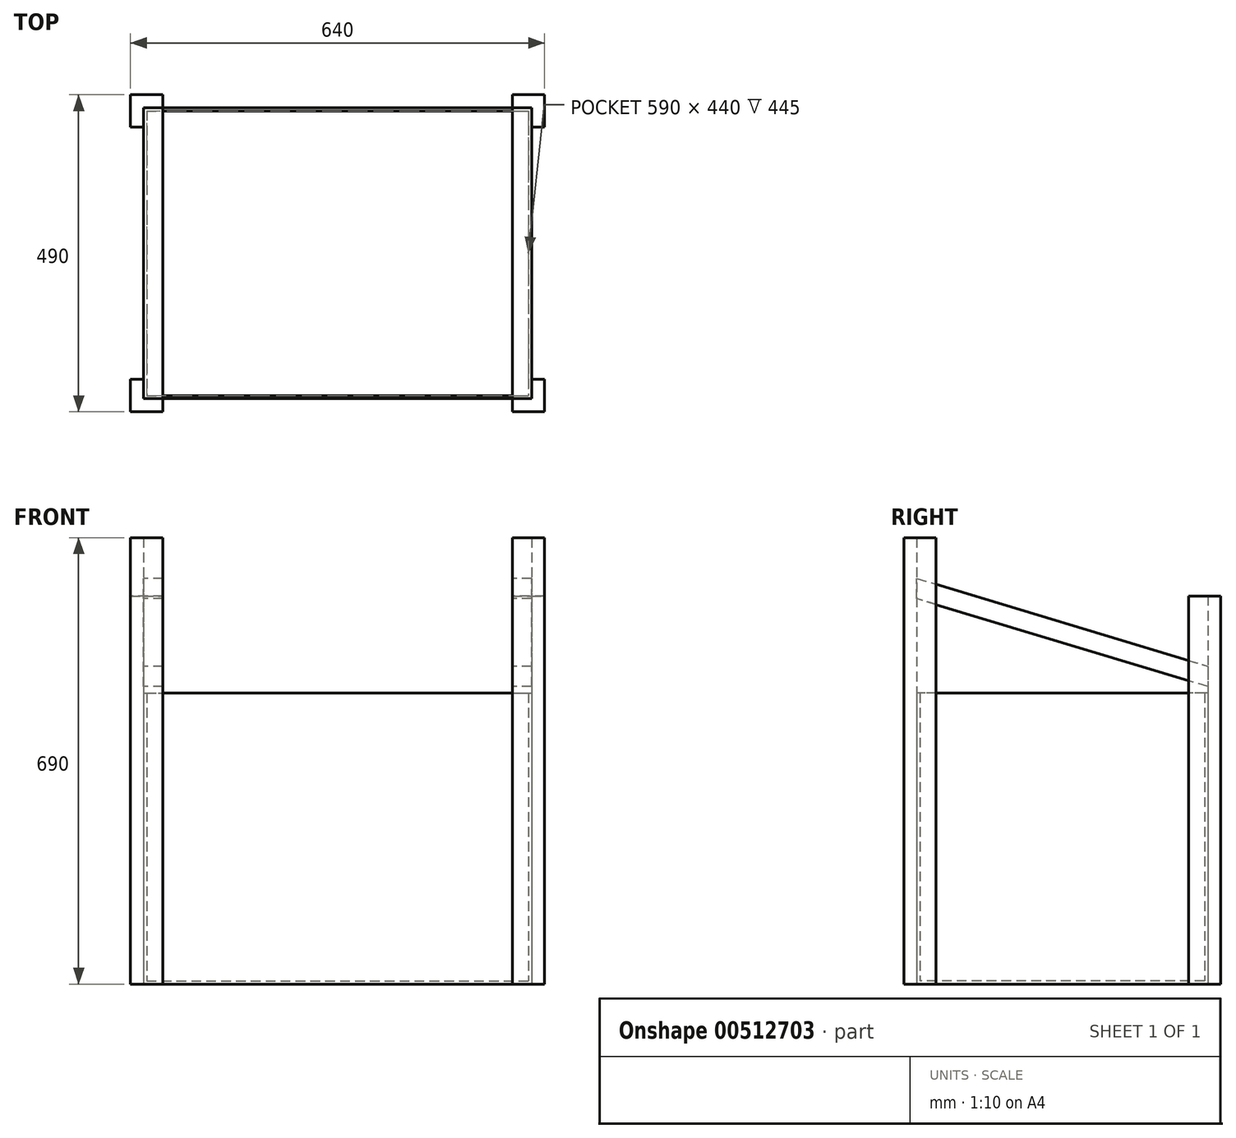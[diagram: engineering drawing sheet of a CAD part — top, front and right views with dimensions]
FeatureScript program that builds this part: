
annotation { "Feature Type Name" : "Feature", "Feature Type Description" : "" }
export const myFeature = defineFeature(function(context is Context, id is Id, definition is map)
    precondition{}
    {
        {
            var Q0;
            Q0=qCreatedBy(makeId("Top.planeOp"),FACE);
            var sketch = newSketch(context, id + "F0", { "sketchPlane" : qUnion([Q0])});
            skLineSegment(sketch, "E0.bottom", {"start": v(-300, 225) * mm, "end": v(300, 225) * mm});
            skLineSegment(sketch, "E0.top", {"start": v(-300, -225) * mm, "end": v(300, -225) * mm});
            skLineSegment(sketch, "E0.left", {"start": v(-300, 225) * mm, "end": v(-300, -225) * mm});
            skLineSegment(sketch, "E0.right", {"start": v(300, 225) * mm, "end": v(300, -225) * mm});
            skPoint(sketch, "E0.middle", {"position": v(0, 0) * mm});
            skSolve(sketch);
        }
        {
            var Q0;
            Q0 = qSketchRegion(id + "F0", true);
            extrude(context, id + "F1", {"entities" : qUnion([Q0]), "depth" : 450 * mm});
        }
        {
            var Q0;
            Q0=makeQuery(id+"F1.opExtrude","CAP_FACE",FACE,{"disambiguationData":[OSD([sQuery(id+"F0.wireOp",EDGE,"E0.bottom"),sQuery(id+"F0.wireOp",EDGE,"E0.top"),sQuery(id+"F0.wireOp",EDGE,"E0.left"),sQuery(id+"F0.wireOp",EDGE,"E0.right")])],"isStart":false});
            shell(context, id + "F2", {"entities" : qUnion([Q0]), "thickness" : 5 * mm});
        }
        {
            var Q0;
            Q0=makeQuery(id+"F1.opExtrude","CAP_FACE",FACE,{"disambiguationData":[OSD([sQuery(id+"F0.wireOp",EDGE,"E0.bottom"),sQuery(id+"F0.wireOp",EDGE,"E0.top"),sQuery(id+"F0.wireOp",EDGE,"E0.left"),sQuery(id+"F0.wireOp",EDGE,"E0.right")])],"isStart":true});
            var sketch = newSketch(context, id + "F3", { "sketchPlane" : qUnion([Q0])});
            skLineSegment(sketch, "E1", {"start": v(-300, 195) * mm, "end": v(-320, 195) * mm});
            skLineSegment(sketch, "E2", {"start": v(-320, 195) * mm, "end": v(-320, 245) * mm});
            skLineSegment(sketch, "E3", {"start": v(-320, 245) * mm, "end": v(-270, 245) * mm});
            skLineSegment(sketch, "E4", {"start": v(-270, 245) * mm, "end": v(-270, 225) * mm});
            skLineSegment(sketch, "E5", {"start": v(-270, 225) * mm, "end": v(-300, 225) * mm});
            skLineSegment(sketch, "E6", {"start": v(-300, 225) * mm, "end": v(-300, 195) * mm});
            skSolve(sketch);
        }
        {
            var Q0;
            Q0 = qSketchRegion(id + "F3", true);
            extrude(context, id + "F4", {"entities" : qUnion([Q0]), "oppositeDirection" : true, "depth" : 690 * mm});
        }
        {
            var Q0;
            Q0=makeQuery(id+"F4.opExtrude","SWEPT_BODY",BODY,{"disambiguationData":[OSD([sQuery(id+"F3.wireOp",EDGE,"E1"),sQuery(id+"F3.wireOp",EDGE,"E2"),sQuery(id+"F3.wireOp",EDGE,"E3"),sQuery(id+"F3.wireOp",EDGE,"E4"),sQuery(id+"F3.wireOp",EDGE,"E5"),sQuery(id+"F3.wireOp",EDGE,"E6")])]});
            transform(context, id + "F5", {"entities" : qUnion([Q0]), "transformType" : TransformType.TRANSLATION_3D, "dx" : 600 * mm, "dy" : 0 * mm, "dz" : 0 * mm, "makeCopy" : true});
        }
        {
            var Q0;
            Q0=makeQuery(id+"F5.opPattern","COPY",BODY,{"derivedFrom":makeQuery(id+"F4.opExtrude","SWEPT_BODY",BODY,{"disambiguationData":[OSD([sQuery(id+"F3.wireOp",EDGE,"E1"),sQuery(id+"F3.wireOp",EDGE,"E2"),sQuery(id+"F3.wireOp",EDGE,"E3"),sQuery(id+"F3.wireOp",EDGE,"E4"),sQuery(id+"F3.wireOp",EDGE,"E5"),sQuery(id+"F3.wireOp",EDGE,"E6")])]}),"instanceName":"1"});
            var Q1;
            Q1=makeQuery(id+"F1.opExtrude","SWEPT_EDGE",EDGE,{"disambiguationData":[OSD([sQuery(id+"F0.wireOp",EDGE,"E0.top"),sQuery(id+"F0.wireOp",EDGE,"E0.right")])]});
            transform(context, id + "F6", {"entities" : qUnion([Q0]), "transformType" : TransformType.ROTATION, "transformAxis" : qUnion([Q1]), "angle" : 90 * degree, "oppositeDirection" : true, "makeCopy" : false});
        }
        {
            var Q0;
            Q0=makeQuery(id+"F1.opExtrude","CAP_FACE",FACE,{"disambiguationData":[OSD([sQuery(id+"F0.wireOp",EDGE,"E0.bottom"),sQuery(id+"F0.wireOp",EDGE,"E0.top"),sQuery(id+"F0.wireOp",EDGE,"E0.left"),sQuery(id+"F0.wireOp",EDGE,"E0.right")])],"isStart":true});
            var sketch = newSketch(context, id + "F7", { "sketchPlane" : qUnion([Q0])});
            skLineSegment(sketch, "E7", {"start": v(300, -195) * mm, "end": v(320, -195) * mm});
            skLineSegment(sketch, "E8", {"start": v(320, -195) * mm, "end": v(320, -245) * mm});
            skLineSegment(sketch, "E9", {"start": v(320, -245) * mm, "end": v(270, -245) * mm});
            skLineSegment(sketch, "E10", {"start": v(270, -245) * mm, "end": v(270, -225) * mm});
            skLineSegment(sketch, "E11", {"start": v(270, -225) * mm, "end": v(300, -225) * mm});
            skLineSegment(sketch, "E12", {"start": v(300, -225) * mm, "end": v(300, -195) * mm});
            skSolve(sketch);
        }
        {
            var Q0;
            Q0 = qSketchRegion(id + "F7", true);
            extrude(context, id + "F8", {"entities" : qUnion([Q0]), "oppositeDirection" : true, "depth" : 600 * mm});
        }
        {
            var Q0;
            Q0=makeQuery(id+"F8.opExtrude","SWEPT_BODY",BODY,{"disambiguationData":[OSD([sQuery(id+"F7.wireOp",EDGE,"E7"),sQuery(id+"F7.wireOp",EDGE,"E8"),sQuery(id+"F7.wireOp",EDGE,"E9"),sQuery(id+"F7.wireOp",EDGE,"E10"),sQuery(id+"F7.wireOp",EDGE,"E11"),sQuery(id+"F7.wireOp",EDGE,"E12")])]});
            transform(context, id + "F9", {"entities" : qUnion([Q0]), "transformType" : TransformType.TRANSLATION_3D, "dx" : -600 * mm, "dy" : 0 * mm, "dz" : 0 * mm, "makeCopy" : true});
        }
        {
            var Q0;
            Q0=makeQuery(id+"F9.opPattern","COPY",BODY,{"derivedFrom":makeQuery(id+"F8.opExtrude","SWEPT_BODY",BODY,{"disambiguationData":[OSD([sQuery(id+"F7.wireOp",EDGE,"E7"),sQuery(id+"F7.wireOp",EDGE,"E8"),sQuery(id+"F7.wireOp",EDGE,"E9"),sQuery(id+"F7.wireOp",EDGE,"E10"),sQuery(id+"F7.wireOp",EDGE,"E11"),sQuery(id+"F7.wireOp",EDGE,"E12")])]}),"instanceName":"1"});
            var Q1;
            Q1=makeQuery(id+"F1.opExtrude","SWEPT_EDGE",EDGE,{"disambiguationData":[OSD([sQuery(id+"F0.wireOp",EDGE,"E0.bottom"),sQuery(id+"F0.wireOp",EDGE,"E0.left")])]});
            transform(context, id + "F10", {"entities" : qUnion([Q0]), "transformType" : TransformType.ROTATION, "transformAxis" : qUnion([Q1]), "angle" : 90 * degree, "oppositeDirection" : true, "makeCopy" : false});
        }
        {
            var Q0;
            Q0=makeQuery(id+"F1.opExtrude","SWEPT_FACE",FACE,{"disambiguationData":[OSD([sQuery(id+"F0.wireOp",EDGE,"E0.left")])]});
            var sketch = newSketch(context, id + "F11", { "sketchPlane" : qUnion([Q0])});
            skLineSegment(sketch, "E13", {"start": v(-225, 460) * mm, "end": v(225, 595.86) * mm});
            skLineSegment(sketch, "E14", {"start": v(225, 595.86) * mm, "end": v(225, 627.2) * mm});
            skLineSegment(sketch, "E15", {"start": v(225, 627.2) * mm, "end": v(-225, 491.34) * mm});
            skLineSegment(sketch, "E16", {"start": v(-225, 491.34) * mm, "end": v(-225, 460) * mm});
            skSolve(sketch);
        }
        {
            var Q0;
            Q0 = qSketchRegion(id + "F11", true);
            extrude(context, id + "F12", {"entities" : qUnion([Q0]), "oppositeDirection" : true, "depth" : 30 * mm});
        }
        {
            var Q0;
            Q0=makeQuery(id+"F12.opExtrude","SWEPT_BODY",BODY,{"disambiguationData":[OSD([sQuery(id+"F11.wireOp",EDGE,"E13"),sQuery(id+"F11.wireOp",EDGE,"E14"),sQuery(id+"F11.wireOp",EDGE,"E15"),sQuery(id+"F11.wireOp",EDGE,"E16")])]});
            transform(context, id + "F13", {"entities" : qUnion([Q0]), "transformType" : TransformType.TRANSLATION_3D, "dx" : 570 * mm, "dy" : 0 * mm, "dz" : 0 * mm, "makeCopy" : true});
        }
    });
